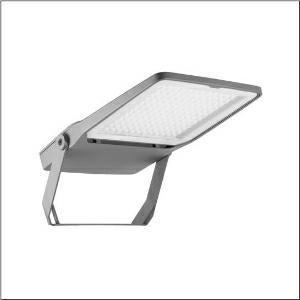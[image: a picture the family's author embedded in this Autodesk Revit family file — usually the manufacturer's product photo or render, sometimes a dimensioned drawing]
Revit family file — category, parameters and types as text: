
# Revit family: floodlight_fl_20_midi___rs17_5xa7682e3b1ac_f763
name_source: partatom
category: Lighting Fixtures
units: mm (PartAtom-declared; Revit-internal decimal feet)

## family parameters
Cut with Voids When Loaded = No
Host = Face
Light Source = No
Part Type = Normal
Room Calculation Point = No
Round Connector Dimension = Use Diameter
Shared = No

## types (1)
- --- (1 x LED 5000K / CRI = 70 (unbekannt), 29600 lm, 5000K)
    Apparent Load = 208 VA
    CIE Flux Codes = 79 92 99 100 100
    Color Rendering = 70
    Color Temperature = 5000K
    Default Elevation = 1800 mm
    Description = Floodlight FL 20 midi, floodlight, primary light control with lens, of plastic, primary optical cover: protective disc, of toughened safety glass, transparent, light distribution: RS17, light emission: direct distribution, primary light characteristic: rotationally symmetric, installation type: surface-mounted, LED High Power LED, rated luminous flux: 29.600 lm, light colour: 750, colour temperature: 5000K, control gear: ECG Plus, control: flexible luminous flux parameterisation, time-dependent luminous flux control, digital communication interface, power reduction, overheat protection, electronic power reduction, with terminal, 5-pole, max. 2.5mm², mains connection: 220..240V, AC, 50/60Hz, rated input power: 208W, LED unit, of diecast aluminium, powder-coated, Siteco® metallic grey (DB 702S), length: 654 mm, width: 450 mm, height: 76mm, housing frame, of diecast aluminium, powder-coated, Siteco® metallic grey (DB 702S), mounting bracket, of steel, powder-coated, Siteco® metallic grey (DB 702S), DALIprotection rating (complete): IP66, insulation class (complete): insulation class II (safety insulation), certification: CE, ENEC, VDE, protection symbol: D, permissible ambient temperature for indoor applications: -40..+40°C, permissible ambient temperature for outdoor applications: -40..+50°C, standard: DIN EN 12944, packaging unit: 1 piece

Light Distribution: RS17
    Height = 76 mm
    Lamp = 1 x LED 5000K / CRI >= 70 (unbekannt)
    Lamp Light Flux = 29600 lm
    Lamp count = 1
    Length = 672 mm
    Luminous efficacy = 142 lm/W
    Manufacturer = Siteco
    ModVariant = No
    Model = 5XA7682E3B1AC
    Number of Poles = 1
    OnlyDefault = Yes
    Power Factor = 1
    Product Name = Floodlight FL 20 midi | RS17
    Product group = floodlight | pylon top
    ProductGroupID = 6101
    Protection Class = Protection class II
    Protection Degree = IP 66
    RLX_Detail_Level = 1
    RlxData = <blob elided: 92169 chars, md5=2f1a68bd>
    Socket = socket
    Standby Power = 0 W
    System Light Flux = 29600 lm
    System Power = 208 W
    Type Comments = factory setting: luminous flux: 100 % | dim-lin: 254 | 484 mA
    Type Image = l_1005943.jpg
    URL = http://relux.com
    VarID = @adj_141741
    Voltage = 0 V
    Weight = 0.00 kg
    Width = 450 mm

## geometry (parser evidence)
native form markers: Blend x4, Sweep x13
no freeform markers — native parametric forms only
